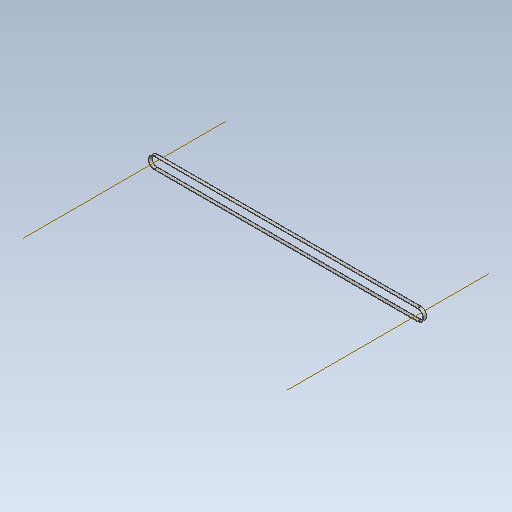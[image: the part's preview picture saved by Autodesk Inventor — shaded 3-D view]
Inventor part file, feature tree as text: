
AUTODESK INVENTOR PART (.ipt)
format: ipt  version: 2020 (Build 240168000, 168)  size: 93,696 bytes
history: native  units: mm (DEFAULTED — no unit token found)
features: other x4, plane x2, sketch x1, sweep x1
ambient origin geometry x8: Origin, YZ Plane, XZ Plane, XY Plane, X Axis, Y Axis, Z Axis, Center Point
bodies: Solid1 (feature_tree)
feature tree (8):
  sketch  "Sketch Path"  dims[d0=4.826mm d2=0.0mm d4=0.254mm d5=0.381mm d6=0.0mm d7=0.0mm d8=0.0mm d9=0.0mm d10=0.0mm d11=0.0mm]
  other  "Cross Section Plane"
  other  "Work Axis1"
  other  "Work Axis2"
  plane  "Work Plane2"
  plane  "Work Plane3"
  sweep  "Belt"
  other  "Cross Section"
